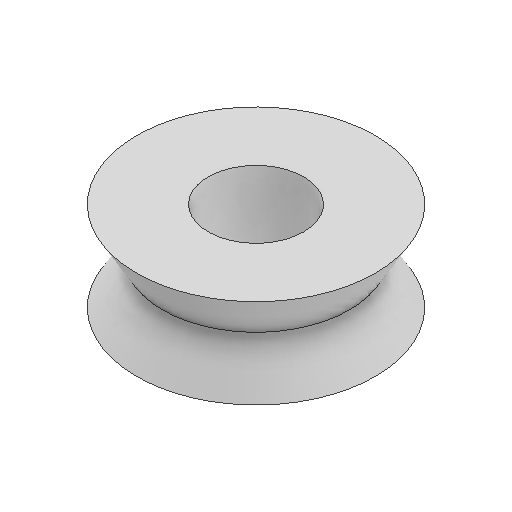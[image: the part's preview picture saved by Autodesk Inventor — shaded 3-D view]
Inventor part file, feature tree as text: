
AUTODESK INVENTOR PART (.ipt)
format: ipt  version: 2025 (Build 290162010, 162A)  size: 110,080 bytes
history: native  units: in
note: dims shown in document units (in); Inventor stores cm internally (conversion verified against a paired STEP export)
features: revolve x1, sketch x1
ambient origin geometry x8: Origin, YZ Plane, XZ Plane, XY Plane, X Axis, Y Axis, Z Axis, Center Point
bodies: Solid1 (feature_tree)
feature tree (2):
  revolve  "Revolution1"  Angle=60.0deg
  sketch  "Sketch1"  dims[d0=0.2in d1=60.0deg d2=0.15in d3=0.08in d4=90.0deg]
